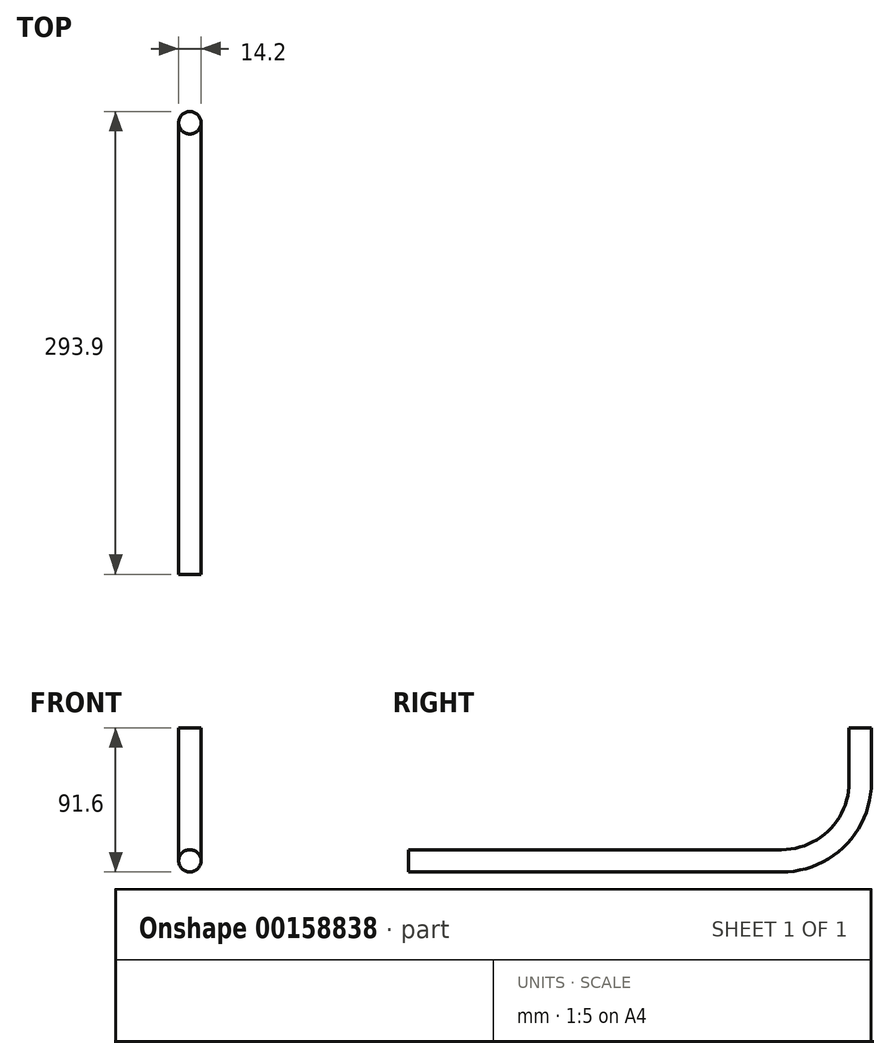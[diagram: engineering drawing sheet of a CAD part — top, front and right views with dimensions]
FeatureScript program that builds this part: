
annotation { "Feature Type Name" : "Feature", "Feature Type Description" : "" }
export const myFeature = defineFeature(function(context is Context, id is Id, definition is map)
    precondition{}
    {
        {
            var Q0;
            Q0=qCreatedBy(makeId("Right.planeOp"),FACE);
            var sketch = newSketch(context, id + "F0", { "sketchPlane" : qUnion([Q0])});
            skLineSegment(sketch, "E0", {"start": v(0, 0) * mm, "end": v(236.8, 0) * mm});
            skLineSegment(sketch, "E1", {"start": v(286.8, 50) * mm, "end": v(286.8, 84.5) * mm});
            skPoint(sketch, "E2.visualSharp", {"position": v(286.8, 0) * mm});
            skArc(sketch, "E2.filletArc", {"start": v(236.8, 0) * mm, "mid": v(272.16, 14.64) * mm, "end": v(286.8, 50) * mm});
            skSolve(sketch);
        }
        {
            var Q0;
            Q0=qCreatedBy(makeId("Front.planeOp"),FACE);
            var sketch = newSketch(context, id + "F1", { "sketchPlane" : qUnion([Q0])});
            skCircle(sketch, "E3", {"center": v(0, 0) * mm, "radius": 7.1 * mm});
            skSolve(sketch);
        }
        {
            var Q0;
            Q0=makeQuery(id+"F1.imprint","IMPRINT",FACE,{"disambiguationData":[TD([[makeQuery(id+"F1.imprint","IMPRINT",EDGE,{"derivedFrom":sQuery(id+"F1.wireOp",EDGE,"E3")}),1.0]])]});
            var Q1;
            Q1=sQuery(id+"F0.wireOp",EDGE,"E0");
            var Q2;
            Q2=sQuery(id+"F0.wireOp",EDGE,"E2.filletArc");
            var Q3;
            Q3=sQuery(id+"F0.wireOp",EDGE,"E1");
            sweep(context, id + "F2", {"profiles" : qUnion([Q0]), "path" : qUnion([Q1, Q2, Q3])});
        }
    });
